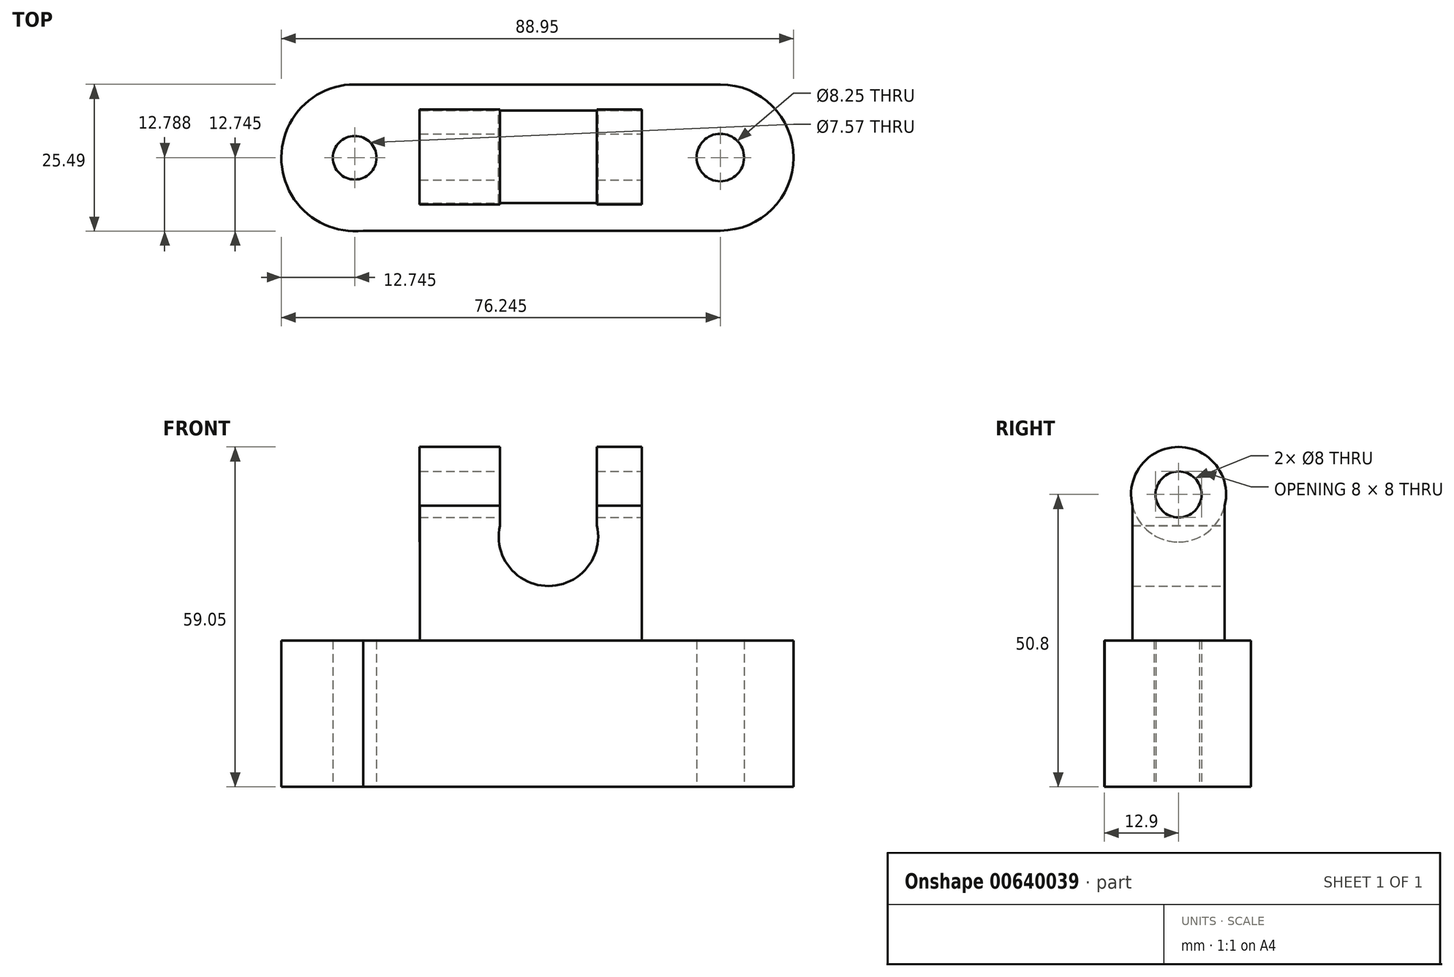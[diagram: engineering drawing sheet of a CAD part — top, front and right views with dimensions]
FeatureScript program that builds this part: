
annotation { "Feature Type Name" : "Feature", "Feature Type Description" : "" }
export const myFeature = defineFeature(function(context is Context, id is Id, definition is map)
    precondition{}
    {
        {
            var Q0;
            Q0=qCreatedBy(makeId("Top.planeOp"),FACE);
            var sketch = newSketch(context, id + "F0", { "sketchPlane" : qUnion([Q0])});
            skLineSegment(sketch, "E0", {"start": v(-33.64, 2.45) * mm, "end": v(-33.64, -22.95) * mm});
            skLineSegment(sketch, "E1", {"start": v(-33.64, -22.95) * mm, "end": v(29.86, -22.95) * mm});
            skLineSegment(sketch, "E2", {"start": v(29.86, -22.95) * mm, "end": v(29.86, 2.45) * mm});
            skLineSegment(sketch, "E3", {"start": v(29.86, 2.45) * mm, "end": v(-33.64, 2.45) * mm});
            skArc(sketch, "E4", {"start": v(-33.64, 2.45) * mm, "mid": v(-46.37, -11.03) * mm, "end": v(-32.17, -22.95) * mm});
            skArc(sketch, "E5", {"start": v(29.86, -22.95) * mm, "mid": v(42.56, -10.25) * mm, "end": v(29.86, 2.45) * mm});
            skCircle(sketch, "E6", {"center": v(-33.64, -10.3) * mm, "radius": 3.79 * mm});
            skCircle(sketch, "E7", {"center": v(29.86, -10.25) * mm, "radius": 4.13 * mm});
            skSolve(sketch);
        }
        {
            var Q0;
            {var subQ0=sQuery(id+"F0.wireOp",EDGE,"E6");var subQ1=sQuery(id+"F0.wireOp",EDGE,"E0");var subQ2=makeQuery(id+"F0.imprint","INTERSECT",VERTEX,{"disambiguationData":[OD(0.0)],"derivedFrom":[subQ1,subQ0]});Q0=makeQuery(id+"F0.imprint","IMPRINT",FACE,{"disambiguationData":[TD([[makeQuery(id+"F0.imprint","IMPRINT",EDGE,{"disambiguationData":[TD([[subQ2,-1.0]])],"derivedFrom":subQ1}),1.0]])]});}
            var Q1;
            {var subQ0=sQuery(id+"F0.wireOp",EDGE,"E7");var subQ1=sQuery(id+"F0.wireOp",EDGE,"E2");var subQ2=makeQuery(id+"F0.imprint","INTERSECT",VERTEX,{"disambiguationData":[OD(0.0)],"derivedFrom":[subQ1,subQ0]});Q1=makeQuery(id+"F0.imprint","IMPRINT",FACE,{"disambiguationData":[TD([[makeQuery(id+"F0.imprint","IMPRINT",EDGE,{"disambiguationData":[TD([[subQ2,-1.0]])],"derivedFrom":subQ1}),1.0]])]});}
            var Q2;
            {var subQ0=sQuery(id+"F0.wireOp",EDGE,"E6");var subQ1=sQuery(id+"F0.wireOp",EDGE,"E0");var subQ2=makeQuery(id+"F0.imprint","INTERSECT",VERTEX,{"disambiguationData":[OD(0.0)],"derivedFrom":[subQ1,subQ0]});Q2=makeQuery(id+"F0.imprint","IMPRINT",FACE,{"disambiguationData":[TD([[makeQuery(id+"F0.imprint","IMPRINT",EDGE,{"disambiguationData":[TD([[subQ2,-1.0]])],"derivedFrom":subQ1}),-1.0]])]});}
            var Q3;
            {var subQ0=sQuery(id+"F0.wireOp",EDGE,"E7");var subQ1=sQuery(id+"F0.wireOp",EDGE,"E2");var subQ2=makeQuery(id+"F0.imprint","INTERSECT",VERTEX,{"disambiguationData":[OD(0.0)],"derivedFrom":[subQ1,subQ0]});Q3=makeQuery(id+"F0.imprint","IMPRINT",FACE,{"disambiguationData":[TD([[makeQuery(id+"F0.imprint","IMPRINT",EDGE,{"disambiguationData":[TD([[subQ2,-1.0]])],"derivedFrom":subQ1}),-1.0]])]});}
            var Q4;
            {var subQ13=sQuery(id+"F0.wireOp",EDGE,"E3");Q4=makeQuery(id+"F0.imprint","IMPRINT",FACE,{"disambiguationData":[TD([[makeQuery(id+"F0.imprint","IMPRINT",EDGE,{"derivedFrom":subQ13}),1.0]])]});}
            var Q5;
            {var subQ0=sQuery(id+"F0.wireOp",EDGE,"E5");Q5=makeQuery(id+"F0.imprint","IMPRINT",FACE,{"disambiguationData":[TD([[makeQuery(id+"F0.imprint","IMPRINT",EDGE,{"derivedFrom":subQ0}),1.0]])]});}
            var Q6;
            {var subQ0=sQuery(id+"F0.wireOp",EDGE,"E4");Q6=makeQuery(id+"F0.imprint","IMPRINT",FACE,{"disambiguationData":[TD([[makeQuery(id+"F0.imprint","IMPRINT",EDGE,{"derivedFrom":subQ0}),1.0]])]});}
            extrude(context, id + "F1", {"entities" : qUnion([Q0, Q1, Q2, Q3, Q4, Q5, Q6]), "depth" : 25.4 * mm, "offsetDistance" : 25.4 * mm});
        }
        {
            var Q0;
            Q0=makeQuery(id+"F1.opExtrude","CAP_FACE",FACE,{"disambiguationData":[OSD([sQuery(id+"F0.wireOp",EDGE,"E1"),sQuery(id+"F0.wireOp",EDGE,"E3"),sQuery(id+"F0.wireOp",EDGE,"E4"),sQuery(id+"F0.wireOp",EDGE,"E5")])],"isStart":false});
            var sketch = newSketch(context, id + "F2", { "sketchPlane" : qUnion([Q0])});
            skCircle(sketch, "E8", {"center": v(-33.64, -10.3) * mm, "radius": 3.59 * mm});
            skCircle(sketch, "E9", {"center": v(29.86, -10.25) * mm, "radius": 4.02 * mm});
            skSolve(sketch);
        }
        {
            var Q0;
            Q0=makeQuery(id+"F2.imprint","IMPRINT",FACE,{"disambiguationData":[TD([[makeQuery(id+"F2.imprint","IMPRINT",EDGE,{"derivedFrom":sQuery(id+"F2.wireOp",EDGE,"E9")}),1.0]])]});
            var Q1;
            Q1=makeQuery(id+"F2.imprint","IMPRINT",FACE,{"disambiguationData":[TD([[makeQuery(id+"F2.imprint","IMPRINT",EDGE,{"derivedFrom":sQuery(id+"F2.wireOp",EDGE,"E8")}),1.0]])]});
            extrude(context, id + "F3", {"entities" : qUnion([Q0, Q1]), "operationType" : NewBodyOperationType.REMOVE, "oppositeDirection" : true, "depth" : 25.4 * mm, "offsetDistance" : 25.4 * mm});
        }
        {
            var Q0;
            Q0=makeQuery(id+"F1.opExtrude","CAP_FACE",FACE,{"disambiguationData":[OSD([sQuery(id+"F0.wireOp",EDGE,"E1"),sQuery(id+"F0.wireOp",EDGE,"E3"),sQuery(id+"F0.wireOp",EDGE,"E4"),sQuery(id+"F0.wireOp",EDGE,"E5")])],"isStart":false});
            var sketch = newSketch(context, id + "F4", { "sketchPlane" : qUnion([Q0])});
            skLineSegment(sketch, "E10", {"start": v(-22.34, -18.16) * mm, "end": v(16.24, -18.16) * mm});
            skLineSegment(sketch, "E11", {"start": v(16.24, -18.16) * mm, "end": v(16.24, -2.12) * mm});
            skLineSegment(sketch, "E12", {"start": v(16.24, -2.12) * mm, "end": v(-22.34, -2.12) * mm});
            skLineSegment(sketch, "E13", {"start": v(-22.34, -2.12) * mm, "end": v(-22.34, -18.16) * mm});
            skSolve(sketch);
        }
        {
            var Q0;
            Q0 = qSketchRegion(id + "F4", true);
            extrude(context, id + "F5", {"entities" : qUnion([Q0]), "operationType" : NewBodyOperationType.ADD, "depth" : 25.4 * mm, "offsetDistance" : 25.4 * mm});
        }
        {
            var Q0;
            Q0=makeQuery(id+"F5.opExtrude","SWEPT_FACE",FACE,{"disambiguationData":[OSD([sQuery(id+"F4.wireOp",EDGE,"E11")])]});
            var sketch = newSketch(context, id + "F6", { "sketchPlane" : qUnion([Q0])});
            skCircle(sketch, "E14", {"center": v(-10.14, 50.8) * mm, "radius": 8.25 * mm});
            skSolve(sketch);
        }
        {
            var Q0;
            Q0 = qSketchRegion(id + "F6", true);
            extrude(context, id + "F7", {"entities" : qUnion([Q0]), "operationType" : NewBodyOperationType.ADD, "oppositeDirection" : true, "depth" : 38.6 * mm, "offsetDistance" : 25.4 * mm});
        }
        {
            var Q0;
            Q0=makeQuery(id+"F7.boolean.opBoolean","MERGE",FACE,{"derivedFrom":[makeQuery(id+"F5.opExtrude","SWEPT_FACE",FACE,{"disambiguationData":[OSD([sQuery(id+"F4.wireOp",EDGE,"E11")])]}),makeQuery(id+"F7.opExtrude","CAP_FACE",FACE,{"disambiguationData":[OSD([sQuery(id+"F6.wireOp",EDGE,"E14")])],"isStart":true})]});
            var sketch = newSketch(context, id + "F8", { "sketchPlane" : qUnion([Q0])});
            skCircle(sketch, "E15", {"center": v(-10.14, 50.8) * mm, "radius": 4 * mm});
            skSolve(sketch);
        }
        {
            var Q0;
            Q0 = qSketchRegion(id + "F8", true);
            extrude(context, id + "F9", {"entities" : qUnion([Q0]), "operationType" : NewBodyOperationType.REMOVE, "oppositeDirection" : true, "depth" : 39.88 * mm, "offsetDistance" : 25.4 * mm});
        }
        {
            var Q0;
            Q0=makeQuery(id+"F5.opExtrude","SWEPT_FACE",FACE,{"disambiguationData":[OSD([sQuery(id+"F4.wireOp",EDGE,"E12")])]});
            var sketch = newSketch(context, id + "F10", { "sketchPlane" : qUnion([Q0])});
            skCircle(sketch, "E16", {"center": v(0, 43.54) * mm, "radius": 8.64 * mm});
            skLineSegment(sketch, "E17", {"start": v(-8.55, 44.79) * mm, "end": v(-8.55, 59.63) * mm});
            skLineSegment(sketch, "E18", {"start": v(8.6, 44.46) * mm, "end": v(8.6, 60.3) * mm});
            skSolve(sketch);
        }
        {
            var Q0;
            {var subQ0=sQuery(id+"F10.wireOp",EDGE,"E16");var subQ1=makeQuery(id+"F7.boolean.opBoolean","INTERSECT",EDGE,{"derivedFrom":[makeQuery(id+"F5.opExtrude","SWEPT_FACE",FACE,{"disambiguationData":[OSD([sQuery(id+"F4.wireOp",EDGE,"E12")])]}),makeQuery(id+"F7.opExtrude","SWEPT_FACE",FACE,{"disambiguationData":[OSD([sQuery(id+"F6.wireOp",EDGE,"E14")])]})]});var subQ2=makeQuery(id+"F10.imprint","INTERSECT",VERTEX,{"disambiguationData":[OD(0.0)],"derivedFrom":[subQ1,subQ0]});Q0=makeQuery(id+"F10.imprint","IMPRINT",FACE,{"disambiguationData":[TD([[makeQuery(id+"F10.imprint","IMPRINT",EDGE,{"disambiguationData":[TD([[subQ2,-1.0]])],"derivedFrom":subQ0}),1.0]])]});}
            var Q1;
            {var subQ0=sQuery(id+"F10.wireOp",EDGE,"E16");var subQ4=makeQuery(id+"F10.imprint","INTERSECT",VERTEX,{"derivedFrom":[subQ0,sQuery(id+"F10.wireOp",EDGE,"E17")]});Q1=makeQuery(id+"F10.imprint","IMPRINT",FACE,{"disambiguationData":[TD([[makeQuery(id+"F10.imprint","IMPRINT",EDGE,{"disambiguationData":[TD([[subQ4,-1.0]])],"derivedFrom":subQ0}),1.0]])]});}
            extrude(context, id + "F11", {"entities" : qUnion([Q0, Q1]), "operationType" : NewBodyOperationType.REMOVE, "oppositeDirection" : true, "depth" : 45.2 * mm, "offsetDistance" : 25.4 * mm});
        }
        {
            var Q0;
            Q0=qCreatedBy(makeId("Front.planeOp"),FACE);
            var sketch = newSketch(context, id + "F12", { "sketchPlane" : qUnion([Q0])});
            skLineSegment(sketch, "E19.bottom", {"start": v(8.43, 42.93) * mm, "end": v(-8.45, 42.93) * mm});
            skLineSegment(sketch, "E19.top", {"start": v(8.43, 63.12) * mm, "end": v(-8.45, 63.12) * mm});
            skLineSegment(sketch, "E19.left", {"start": v(8.43, 42.93) * mm, "end": v(8.43, 63.12) * mm});
            skLineSegment(sketch, "E19.right", {"start": v(-8.45, 42.93) * mm, "end": v(-8.45, 63.12) * mm});
            skSolve(sketch);
        }
        {
            var Q0;
            Q0=makeQuery(id+"F12.imprint","IMPRINT",FACE,{"disambiguationData":[TD([[makeQuery(id+"F12.imprint","IMPRINT",EDGE,{"derivedFrom":sQuery(id+"F12.wireOp",EDGE,"E19.bottom")}),-1.0]])]});
            extrude(context, id + "F13", {"entities" : qUnion([Q0]), "operationType" : NewBodyOperationType.REMOVE, "depth" : 34.3 * mm, "offsetDistance" : 25.4 * mm});
        }
    });
